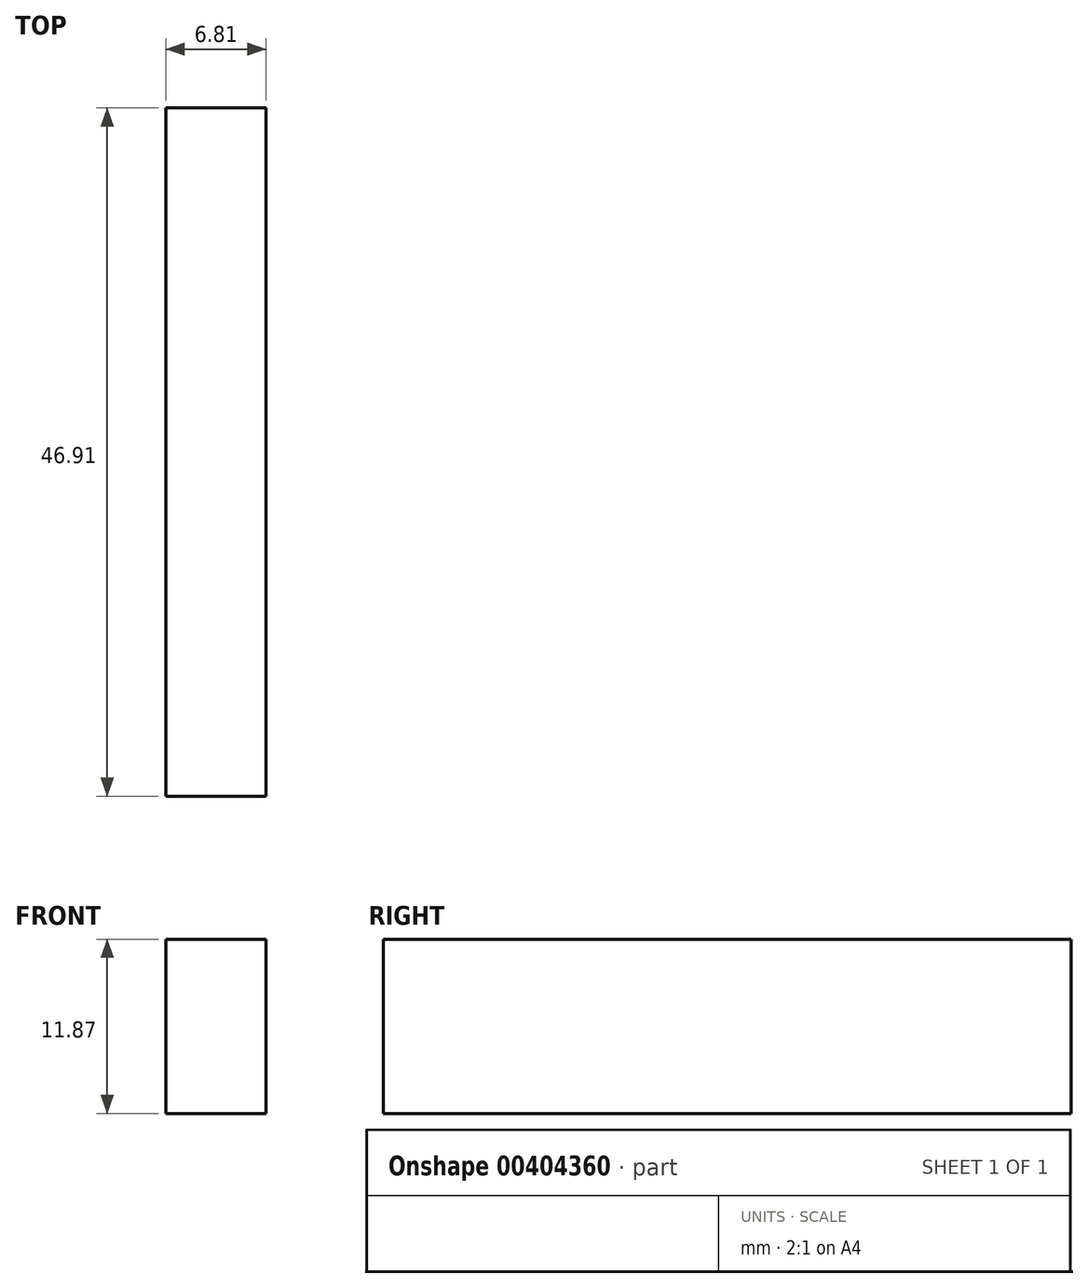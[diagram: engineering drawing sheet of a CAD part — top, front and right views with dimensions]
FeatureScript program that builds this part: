
annotation { "Feature Type Name" : "Feature", "Feature Type Description" : "" }
export const myFeature = defineFeature(function(context is Context, id is Id, definition is map)
    precondition{}
    {
        {
            var Q0;
            Q0=qCreatedBy(makeId("Right.planeOp"),FACE);
            var sketch = newSketch(context, id + "F0", { "sketchPlane" : qUnion([Q0])});
            skCircle(sketch, "E0", {"center": v(16.65, 141.45) * mm, "radius": 16.5 * mm, "construction": true});
            skLineSegment(sketch, "E1", {"start": v(16.65, 141.45) * mm, "end": v(16.65, 141.45) * mm});
            skLineSegment(sketch, "E2", {"start": v(16.65, 141.45) * mm, "end": v(16.65, 146.64) * mm});
            skLineSegment(sketch, "E3", {"start": v(16.65, 146.64) * mm, "end": v(63.56, 146.64) * mm});
            skLineSegment(sketch, "E4", {"start": v(63.56, 146.64) * mm, "end": v(63.56, 134.77) * mm});
            skLineSegment(sketch, "E5", {"start": v(63.56, 134.77) * mm, "end": v(16.65, 134.77) * mm});
            skLineSegment(sketch, "E6", {"start": v(16.65, 134.77) * mm, "end": v(16.65, 141.45) * mm});
            skSolve(sketch);
        }
        {
            var Q0;
            Q0=makeQuery(id+"F0.imprint","IMPRINT",FACE,{"disambiguationData":[TD([[makeQuery(id+"F0.imprint","IMPRINT",EDGE,{"derivedFrom":sQuery(id+"F0.wireOp",EDGE,"E2")}),-1.0]])]});
            var sketch = newSketch(context, id + "F1", { "sketchPlane" : qUnion([Q0])});
            skSolve(sketch);
        }
        {
            var Q0;
            Q0 = qSketchRegion(id + "F1", true);
            var Q1;
            Q1=makeQuery(id+"F0.imprint","IMPRINT",FACE,{"disambiguationData":[TD([[makeQuery(id+"F0.imprint","IMPRINT",EDGE,{"derivedFrom":sQuery(id+"F0.wireOp",EDGE,"E2")}),-1.0]])]});
            extrude(context, id + "F2", {"entities" : qUnion([Q0, Q1]), "depth" : 6.8 * mm});
        }
    });
